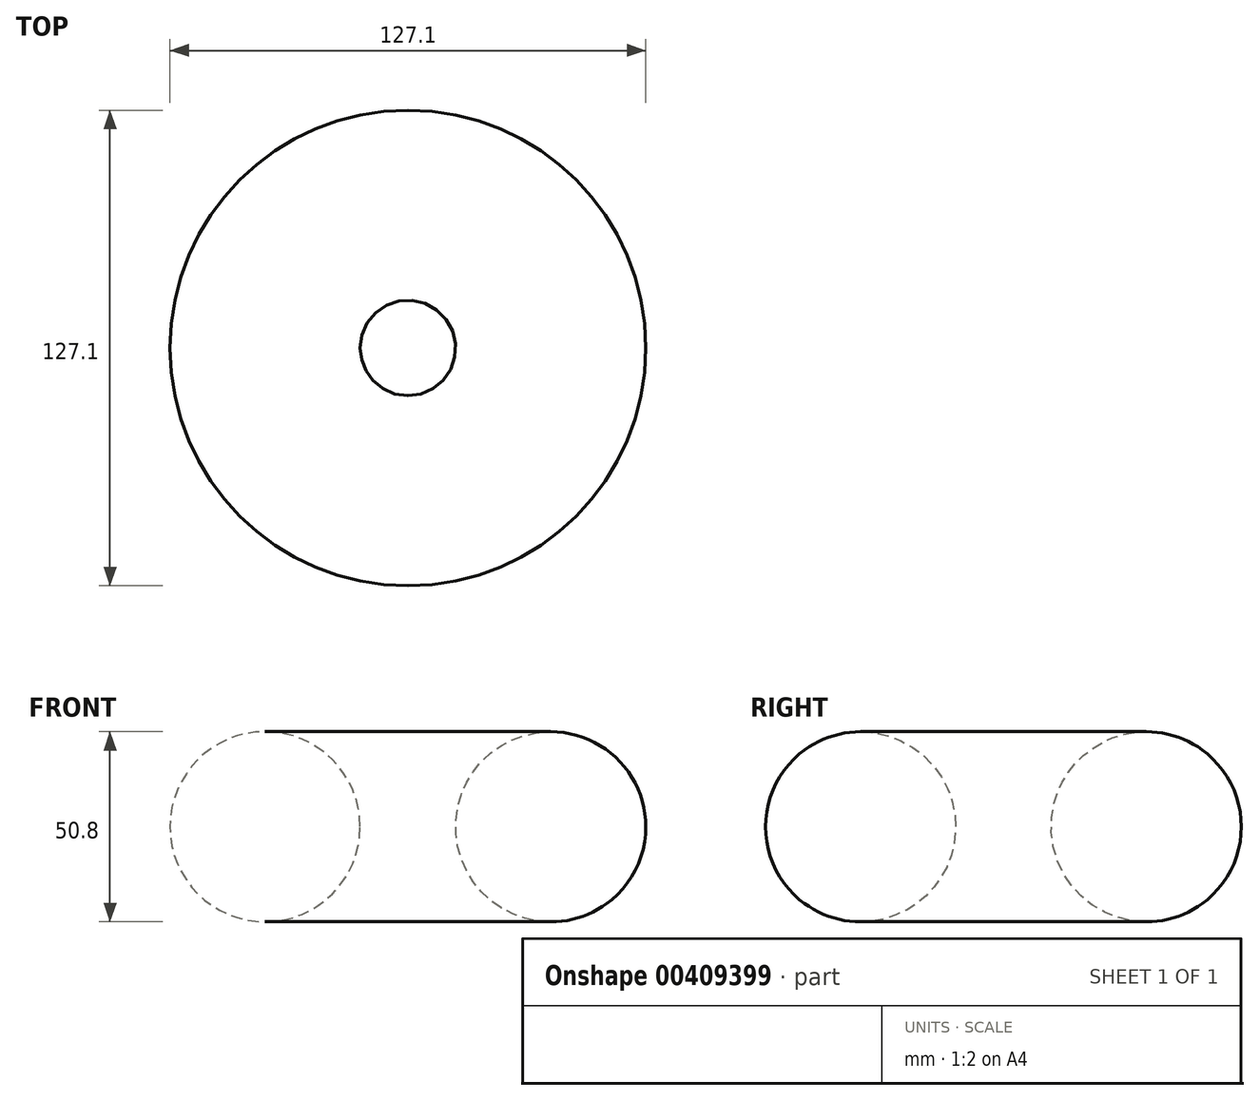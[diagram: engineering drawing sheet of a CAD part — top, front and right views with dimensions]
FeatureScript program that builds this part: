
annotation { "Feature Type Name" : "Feature", "Feature Type Description" : "" }
export const myFeature = defineFeature(function(context is Context, id is Id, definition is map)
    precondition{}
    {
        {
            var Q0;
            Q0=qCreatedBy(makeId("Front.planeOp"),FACE);
            var sketch = newSketch(context, id + "F0", { "sketchPlane" : qUnion([Q0])});
            skLineSegment(sketch, "E0", {"start": v(-38.15, 4.38) * mm, "end": v(-38.15, 57.93) * mm, "construction": true});
            skCircle(sketch, "E1", {"center": v(0, 0) * mm, "radius": 25.4 * mm});
            skSolve(sketch);
        }
        {
            var Q0;
            Q0=makeQuery(id+"F0.imprint","IMPRINT",FACE,{"disambiguationData":[TD([[makeQuery(id+"F0.imprint","IMPRINT",EDGE,{"derivedFrom":sQuery(id+"F0.wireOp",EDGE,"E1")}),1.0]])]});
            var Q1;
            Q1=sQuery(id+"F0.wireOp",EDGE,"E1");
            var Q2;
            Q2=sQuery(id+"F0.wireOp",EDGE,"E0");
            revolve(context, id + "F1", {"entities" : qUnion([Q0]), "surfaceEntities" : qUnion([Q1]), "axis" : qUnion([Q2]), "revolveType" : RevolveType.FULL});
        }
    });
